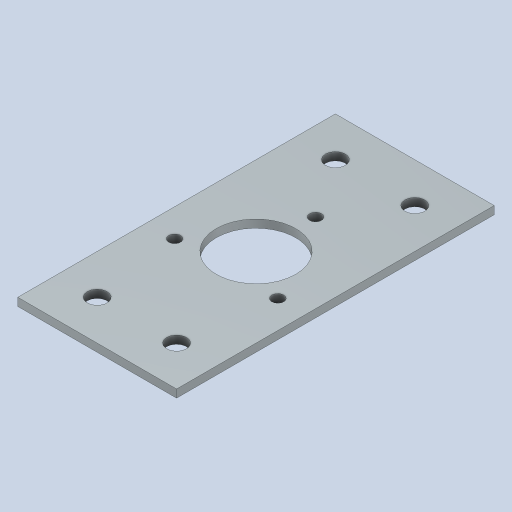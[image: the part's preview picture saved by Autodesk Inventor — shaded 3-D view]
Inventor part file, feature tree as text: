
AUTODESK INVENTOR PART (.ipt)
format: ipt  version: 2023 (Build 270158000, 158)  size: 143,360 bytes
history: native  units: mm
features: other x1, extrude x1, sketch x1
ambient origin geometry x8: Origin, YZ Plane, XZ Plane, XY Plane, X Axis, Y Axis, Z Axis, Center Point
bodies: Body1 (feature_tree)
feature tree (3):
  other  "Sólido1"
  extrude  "Extrusão1"  Depth=80.0mm
  sketch  "Esboço1"  dims[d0=40.0mm d1=80.0mm d2=2.0mm d3=0.0mm d19=40.0mm d20=10.0mm d21=10.0mm d60=5.0mm d61=10.0mm d63=20.0mm d64=10.0mm d65=10.0mm d66=20.0mm d67=20.0mm d68=3.0mm d69=15.0mm d70=30.0mm d72=360.0deg]
